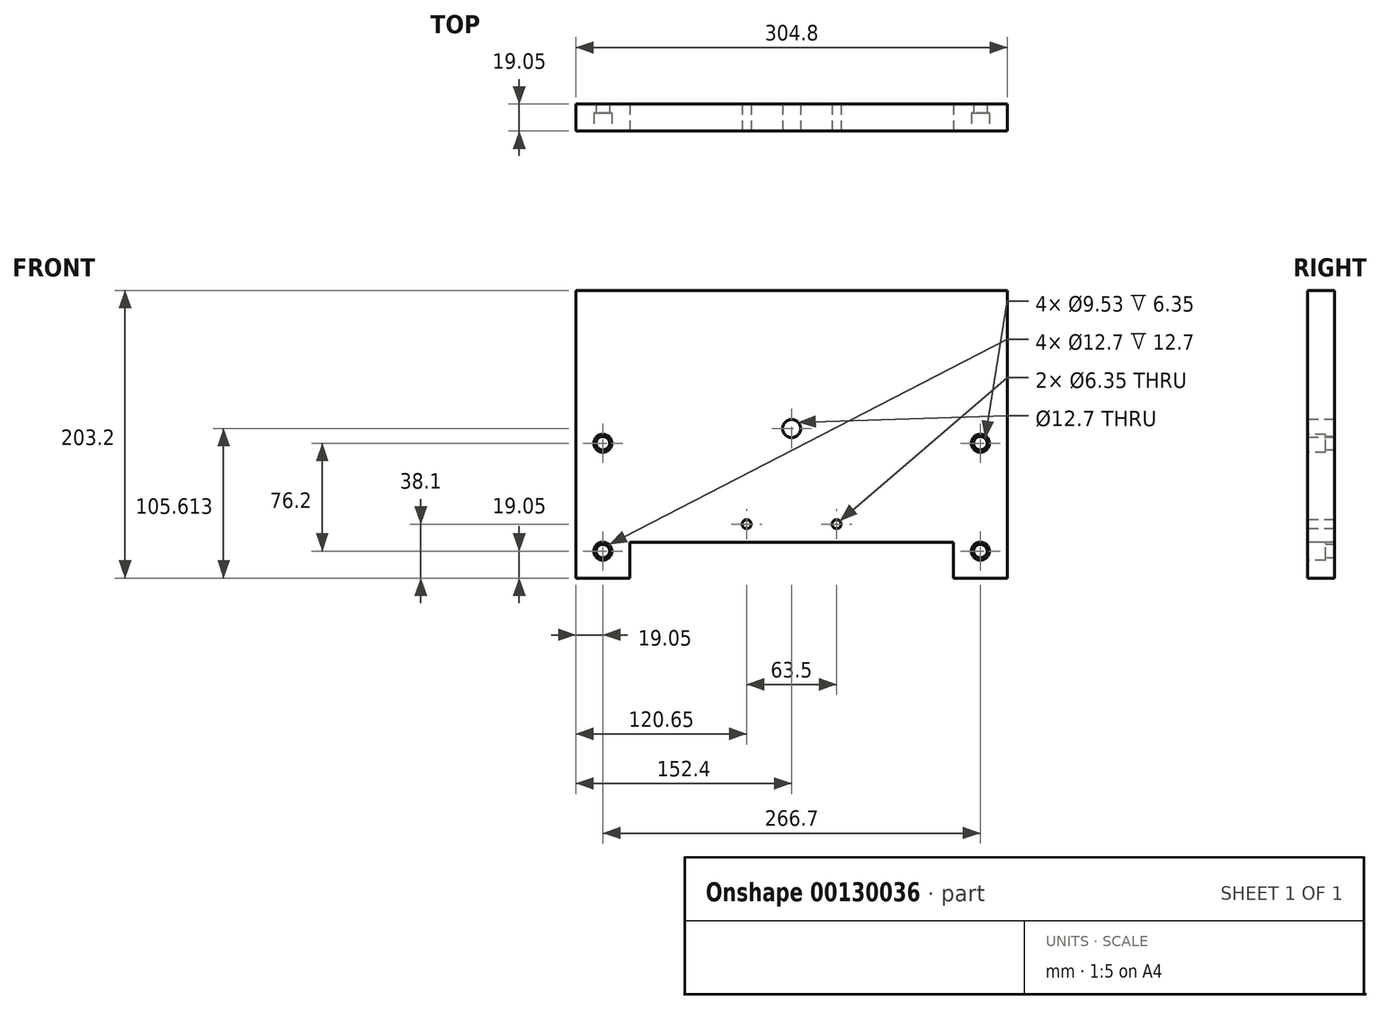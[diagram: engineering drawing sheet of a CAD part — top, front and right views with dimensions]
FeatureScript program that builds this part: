
annotation { "Feature Type Name" : "Feature", "Feature Type Description" : "" }
export const myFeature = defineFeature(function(context is Context, id is Id, definition is map)
    precondition{}
    {
        {
            var Q0;
            Q0=qCreatedBy(makeId("Front.planeOp"),FACE);
            var sketch = newSketch(context, id + "F0", { "sketchPlane" : qUnion([Q0])});
            skLineSegment(sketch, "E0.bottom", {"start": v(0, 0) * mm, "end": v(304.8, 0) * mm});
            skLineSegment(sketch, "E0.top", {"start": v(0, 203.2) * mm, "end": v(304.8, 203.2) * mm});
            skLineSegment(sketch, "E0.left", {"start": v(0, 0) * mm, "end": v(0, 203.2) * mm});
            skLineSegment(sketch, "E0.right", {"start": v(304.8, 0) * mm, "end": v(304.8, 203.2) * mm});
            skSolve(sketch);
        }
        {
            var Q0;
            Q0=makeQuery(id+"F0.imprint","IMPRINT",FACE,{"disambiguationData":[TD([[makeQuery(id+"F0.imprint","IMPRINT",EDGE,{"derivedFrom":sQuery(id+"F0.wireOp",EDGE,"E0.bottom")}),1.0]])]});
            extrude(context, id + "F1", {"entities" : qUnion([Q0]), "depth" : 19.05 * mm});
        }
        {
            var Q0;
            Q0=makeQuery(id+"F1.opExtrude","CAP_FACE",FACE,{"disambiguationData":[OSD([sQuery(id+"F0.wireOp",EDGE,"E0.bottom"),sQuery(id+"F0.wireOp",EDGE,"E0.top"),sQuery(id+"F0.wireOp",EDGE,"E0.left"),sQuery(id+"F0.wireOp",EDGE,"E0.right")])],"isStart":false});
            var sketch = newSketch(context, id + "F2", { "sketchPlane" : qUnion([Q0])});
            skLineSegment(sketch, "E1.bottom", {"start": v(38.1, 0) * mm, "end": v(266.7, 0) * mm});
            skLineSegment(sketch, "E1.top", {"start": v(38.1, 25.4) * mm, "end": v(266.7, 25.4) * mm});
            skLineSegment(sketch, "E1.left", {"start": v(38.1, 0) * mm, "end": v(38.1, 25.4) * mm});
            skLineSegment(sketch, "E1.right", {"start": v(266.7, 0) * mm, "end": v(266.7, 25.4) * mm});
            skSolve(sketch);
        }
        {
            var Q0;
            Q0 = qSketchRegion(id + "F2", true);
            extrude(context, id + "F3", {"entities" : qUnion([Q0]), "operationType" : NewBodyOperationType.REMOVE, "endBound" : BoundingType.THROUGH_ALL, "oppositeDirection" : true, "depth" : 25.4 * mm});
        }
        {
            var Q0;
            Q0=makeQuery(id+"F1.opExtrude","CAP_FACE",FACE,{"disambiguationData":[OSD([sQuery(id+"F0.wireOp",EDGE,"E0.bottom"),sQuery(id+"F0.wireOp",EDGE,"E0.top"),sQuery(id+"F0.wireOp",EDGE,"E0.left"),sQuery(id+"F0.wireOp",EDGE,"E0.right")])],"isStart":false});
            var sketch = newSketch(context, id + "F4", { "sketchPlane" : qUnion([Q0])});
            skPoint(sketch, "E2", {"position": v(120.65, 38.1) * mm});
            skPoint(sketch, "E3", {"position": v(184.15, 38.1) * mm});
            skSolve(sketch);
        }
        {
            var Q0;
            Q0=sQuery(id+"F4.wireOp",VERTEX,"E2");
            var Q1;
            Q1=sQuery(id+"F4.wireOp",VERTEX,"E3");
            var Q2;
            Q2=makeQuery(id+"F1.opExtrude","SWEPT_BODY",BODY,{"disambiguationData":[OSD([sQuery(id+"F0.wireOp",EDGE,"E0.bottom"),sQuery(id+"F0.wireOp",EDGE,"E0.top"),sQuery(id+"F0.wireOp",EDGE,"E0.left"),sQuery(id+"F0.wireOp",EDGE,"E0.right")])]});
            hole(context, id + "F5", {"style" : HoleStyle.SIMPLE, "endStyle" : HoleEndStyle.THROUGH, "holeDiameter" : 6.35 * mm, "locations" : qUnion([Q0, Q1]), "scope" : qUnion([Q2]), "isTappedThrough" : true});
        }
        {
            var Q0;
            Q0=makeQuery(id+"F1.opExtrude","CAP_FACE",FACE,{"disambiguationData":[OSD([sQuery(id+"F0.wireOp",EDGE,"E0.bottom"),sQuery(id+"F0.wireOp",EDGE,"E0.top"),sQuery(id+"F0.wireOp",EDGE,"E0.left"),sQuery(id+"F0.wireOp",EDGE,"E0.right")])],"isStart":false});
            var sketch = newSketch(context, id + "F6", { "sketchPlane" : qUnion([Q0])});
            skPoint(sketch, "E4", {"position": v(152.4, 105.61) * mm});
            skPoint(sketch, "E4.positionSnap0", {"position": v(152.4, 25.4) * mm});
            skSolve(sketch);
        }
        {
            var Q0;
            Q0=sQuery(id+"F6.wireOp",VERTEX,"E4");
            var Q1;
            Q1=makeQuery(id+"F1.opExtrude","SWEPT_BODY",BODY,{"disambiguationData":[OSD([sQuery(id+"F0.wireOp",EDGE,"E0.bottom"),sQuery(id+"F0.wireOp",EDGE,"E0.top"),sQuery(id+"F0.wireOp",EDGE,"E0.left"),sQuery(id+"F0.wireOp",EDGE,"E0.right")])]});
            hole(context, id + "F7", {"style" : HoleStyle.SIMPLE, "endStyle" : HoleEndStyle.THROUGH, "holeDiameter" : 12.7 * mm, "locations" : qUnion([Q0]), "scope" : qUnion([Q1]), "isTappedThrough" : true});
        }
        {
            var Q0;
            Q0=makeQuery(id+"F1.opExtrude","CAP_FACE",FACE,{"disambiguationData":[OSD([sQuery(id+"F0.wireOp",EDGE,"E0.bottom"),sQuery(id+"F0.wireOp",EDGE,"E0.top"),sQuery(id+"F0.wireOp",EDGE,"E0.left"),sQuery(id+"F0.wireOp",EDGE,"E0.right")])],"isStart":false});
            var sketch = newSketch(context, id + "F8", { "sketchPlane" : qUnion([Q0])});
            skPoint(sketch, "E5", {"position": v(19.05, 19.05) * mm});
            skPoint(sketch, "E6", {"position": v(19.05, 95.25) * mm});
            skPoint(sketch, "E7", {"position": v(285.75, 19.05) * mm});
            skPoint(sketch, "E8", {"position": v(285.75, 95.25) * mm});
            skSolve(sketch);
        }
        {
            var Q0;
            Q0=sQuery(id+"F8.wireOp",VERTEX,"E5");
            var Q1;
            Q1=sQuery(id+"F8.wireOp",VERTEX,"E6");
            var Q2;
            Q2=sQuery(id+"F8.wireOp",VERTEX,"E7");
            var Q3;
            Q3=sQuery(id+"F8.wireOp",VERTEX,"E8");
            var Q4;
            Q4=makeQuery(id+"F1.opExtrude","SWEPT_BODY",BODY,{"disambiguationData":[OSD([sQuery(id+"F0.wireOp",EDGE,"E0.bottom"),sQuery(id+"F0.wireOp",EDGE,"E0.top"),sQuery(id+"F0.wireOp",EDGE,"E0.left"),sQuery(id+"F0.wireOp",EDGE,"E0.right")])]});
            hole(context, id + "F9", {"style" : HoleStyle.C_BORE, "endStyle" : HoleEndStyle.THROUGH, "holeDiameter" : 9.52 * mm, "cBoreDiameter" : 12.7 * mm, "cBoreDepth" : 12.7 * mm, "locations" : qUnion([Q0, Q1, Q2, Q3]), "scope" : qUnion([Q4]), "isTappedThrough" : true});
        }
    });
